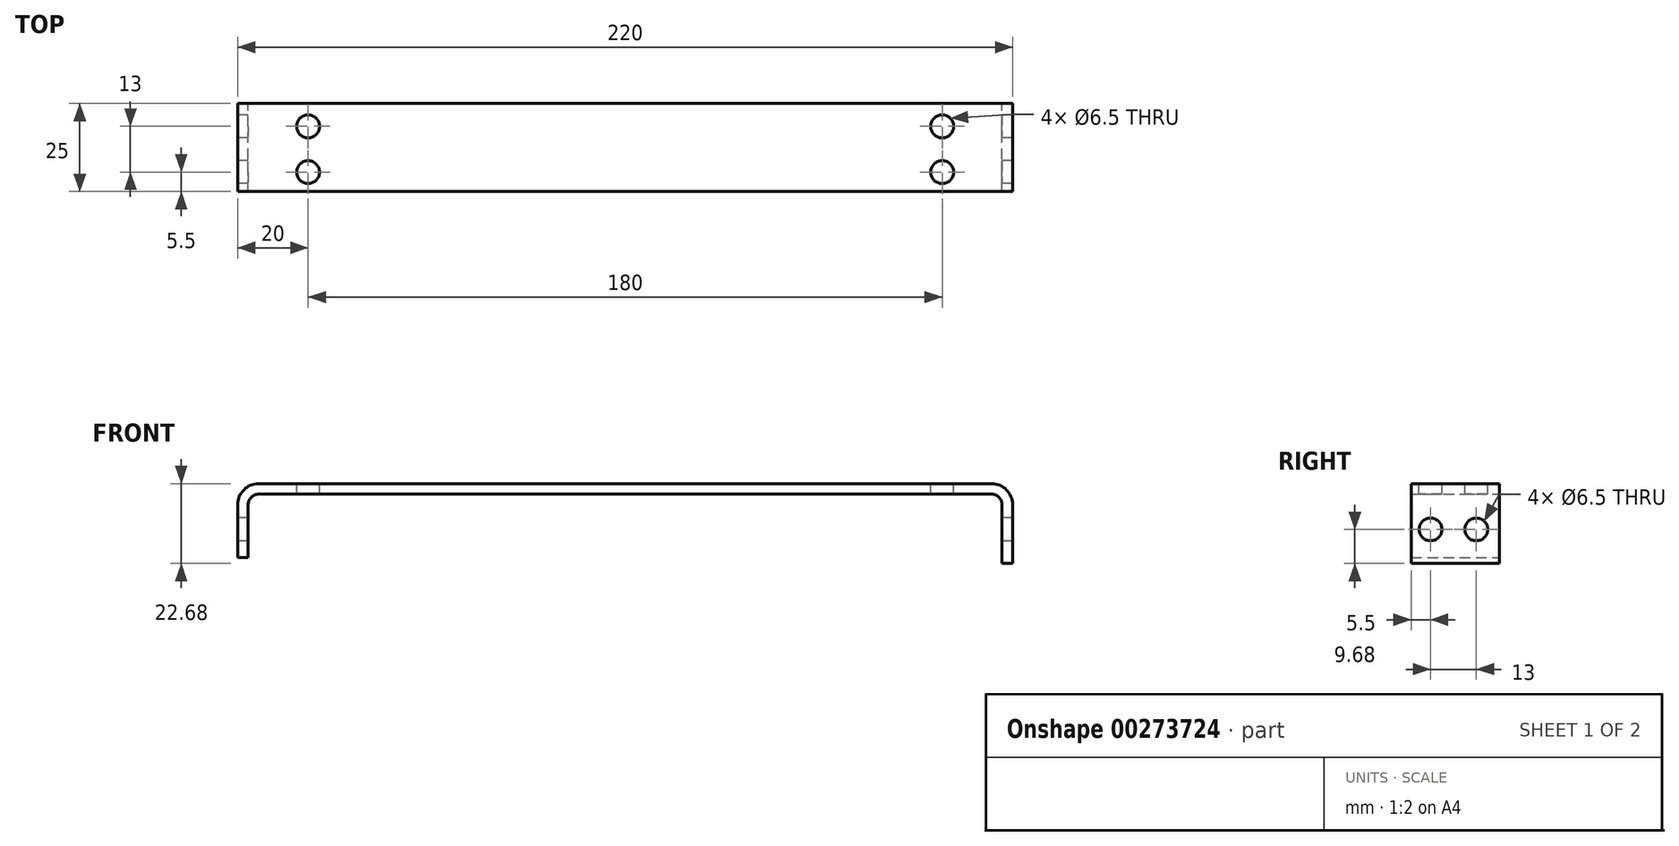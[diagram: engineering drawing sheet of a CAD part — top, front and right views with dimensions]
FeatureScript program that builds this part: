
annotation { "Feature Type Name" : "Feature", "Feature Type Description" : "" }
export const myFeature = defineFeature(function(context is Context, id is Id, definition is map)
    precondition{}
    {
        {
            var Q0;
            Q0=qCreatedBy(makeId("Front.planeOp"),FACE);
            var sketch = newSketch(context, id + "F0", { "sketchPlane" : qUnion([Q0])});
            skLineSegment(sketch, "E0.bottom", {"start": v(-110, 1.5) * mm, "end": v(110, 1.5) * mm});
            skLineSegment(sketch, "E0.top", {"start": v(-110, -1.5) * mm, "end": v(110, -1.5) * mm});
            skLineSegment(sketch, "E0.left", {"start": v(-110, 1.5) * mm, "end": v(-110, -1.5) * mm});
            skLineSegment(sketch, "E0.right", {"start": v(110, 1.5) * mm, "end": v(110, -1.5) * mm});
            skPoint(sketch, "E0.middle", {"position": v(0, 0) * mm});
            skLineSegment(sketch, "E1.bottom", {"start": v(-110, -1.5) * mm, "end": v(-107, -1.5) * mm});
            skLineSegment(sketch, "E1.top", {"start": v(-110, -19.5) * mm, "end": v(-107, -19.5) * mm});
            skLineSegment(sketch, "E1.left", {"start": v(-110, -1.5) * mm, "end": v(-110, -19.5) * mm});
            skLineSegment(sketch, "E1.right", {"start": v(-107, -1.5) * mm, "end": v(-107, -19.5) * mm});
            skLineSegment(sketch, "E2.bottom", {"start": v(110, -1.5) * mm, "end": v(107, -1.5) * mm});
            skLineSegment(sketch, "E2.top", {"start": v(110, -21.18) * mm, "end": v(107, -21.18) * mm});
            skLineSegment(sketch, "E2.left", {"start": v(110, -1.5) * mm, "end": v(110, -21.18) * mm});
            skLineSegment(sketch, "E2.right", {"start": v(107, -1.5) * mm, "end": v(107, -21.18) * mm});
            skSolve(sketch);
        }
        {
            var Q0;
            Q0 = qSketchRegion(id + "F0", true);
            extrude(context, id + "F1", {"entities" : qUnion([Q0]), "depth" : 25 * mm});
        }
        {
            var Q0;
            Q0=makeQuery(id+"F1.opExtrude","SWEPT_FACE",FACE,{"disambiguationData":[OSD([sQuery(id+"F0.wireOp",EDGE,"E0.bottom")])]});
            var sketch = newSketch(context, id + "F2", { "sketchPlane" : qUnion([Q0])});
            skLineSegment(sketch, "E3", {"start": v(-90, 0) * mm, "end": v(-90, -25) * mm, "construction": true});
            skPoint(sketch, "E4", {"position": v(-90, -6.5) * mm});
            skPoint(sketch, "E5", {"position": v(-90, -19.5) * mm});
            skPoint(sketch, "E6.MirrorP", {"position": v(90, -6.5) * mm});
            skPoint(sketch, "E7.MirrorP", {"position": v(90, -19.5) * mm});
            skSolve(sketch);
        }
        {
            var Q0;
            Q0=makeQuery(id+"F1.opExtrude","SWEPT_FACE",FACE,{"disambiguationData":[OSD([sQuery(id+"F0.wireOp",EDGE,"E0.left"),sQuery(id+"F0.wireOp",EDGE,"E1.left")])]});
            var sketch = newSketch(context, id + "F3", { "sketchPlane" : qUnion([Q0])});
            skLineSegment(sketch, "E8", {"start": v(0, -11.5) * mm, "end": v(25, -11.5) * mm, "construction": true});
            skPoint(sketch, "E9", {"position": v(6.5, -11.5) * mm});
            skPoint(sketch, "E10", {"position": v(19.5, -11.5) * mm});
            skSolve(sketch);
        }
        {
            var Q0;
            Q0=sQuery(id+"F2.wireOp",VERTEX,"E5");
            var Q1;
            Q1=sQuery(id+"F2.wireOp",VERTEX,"E4");
            var Q2;
            Q2=sQuery(id+"F2.wireOp",VERTEX,"E6.MirrorP");
            var Q3;
            Q3=sQuery(id+"F2.wireOp",VERTEX,"E7.MirrorP");
            var Q4;
            Q4=makeQuery(id+"F1.opExtrude","SWEPT_BODY",BODY,{"disambiguationData":[OSD([sQuery(id+"F0.wireOp",EDGE,"E0.bottom"),sQuery(id+"F0.wireOp",EDGE,"E0.top"),sQuery(id+"F0.wireOp",EDGE,"E0.left"),sQuery(id+"F0.wireOp",EDGE,"E0.right"),sQuery(id+"F0.wireOp",EDGE,"E1.top"),sQuery(id+"F0.wireOp",EDGE,"E1.left"),sQuery(id+"F0.wireOp",EDGE,"E1.right"),sQuery(id+"F0.wireOp",EDGE,"E2.top"),sQuery(id+"F0.wireOp",EDGE,"E2.left"),sQuery(id+"F0.wireOp",EDGE,"E2.right")])]});
            hole(context, id + "F4", {"style" : HoleStyle.SIMPLE, "endStyle" : HoleEndStyle.THROUGH, "holeDiameter" : 6.5 * mm, "tappedDepth" : 12 * mm, "tapClearance" : 3, "locations" : qUnion([Q0, Q1, Q2, Q3]), "scope" : qUnion([Q4])});
        }
        {
            var Q0;
            Q0=sQuery(id+"F3.wireOp",VERTEX,"E10");
            var Q1;
            Q1=sQuery(id+"F3.wireOp",VERTEX,"E9");
            var Q2;
            Q2=makeQuery(id+"F1.opExtrude","SWEPT_BODY",BODY,{"disambiguationData":[OSD([sQuery(id+"F0.wireOp",EDGE,"E0.bottom"),sQuery(id+"F0.wireOp",EDGE,"E0.top"),sQuery(id+"F0.wireOp",EDGE,"E0.left"),sQuery(id+"F0.wireOp",EDGE,"E0.right"),sQuery(id+"F0.wireOp",EDGE,"E1.top"),sQuery(id+"F0.wireOp",EDGE,"E1.left"),sQuery(id+"F0.wireOp",EDGE,"E1.right"),sQuery(id+"F0.wireOp",EDGE,"E2.top"),sQuery(id+"F0.wireOp",EDGE,"E2.left"),sQuery(id+"F0.wireOp",EDGE,"E2.right")])]});
            hole(context, id + "F5", {"style" : HoleStyle.SIMPLE, "endStyle" : HoleEndStyle.THROUGH, "holeDiameter" : 6.5 * mm, "tappedDepth" : 12 * mm, "tapClearance" : 3, "locations" : qUnion([Q0, Q1]), "scope" : qUnion([Q2])});
        }
        {
            var Q0;
            Q0=makeQuery(id+"F1.opExtrude","SWEPT_EDGE",EDGE,{"disambiguationData":[OSD([sQuery(id+"F0.wireOp",EDGE,"E0.top"),sQuery(id+"F0.wireOp",EDGE,"E1.bottom"),sQuery(id+"F0.wireOp",EDGE,"E1.right")])]});
            var Q1;
            Q1=makeQuery(id+"F1.opExtrude","SWEPT_EDGE",EDGE,{"disambiguationData":[OSD([sQuery(id+"F0.wireOp",EDGE,"E0.top"),sQuery(id+"F0.wireOp",EDGE,"E2.bottom"),sQuery(id+"F0.wireOp",EDGE,"E2.right")])]});
            fillet(context, id + "F6", {"entities" : qUnion([Q0, Q1]), "radius" : 3 * mm, "tangentPropagation" : true, "allowEdgeOverflow" : false});
        }
        {
            var Q0;
            Q0=makeQuery(id+"F1.opExtrude","SWEPT_EDGE",EDGE,{"disambiguationData":[OSD([sQuery(id+"F0.wireOp",EDGE,"E0.bottom"),sQuery(id+"F0.wireOp",EDGE,"E0.left")])]});
            var Q1;
            Q1=makeQuery(id+"F1.opExtrude","SWEPT_EDGE",EDGE,{"disambiguationData":[OSD([sQuery(id+"F0.wireOp",EDGE,"E0.bottom"),sQuery(id+"F0.wireOp",EDGE,"E0.right")])]});
            fillet(context, id + "F7", {"entities" : qUnion([Q0, Q1]), "radius" : 6 * mm, "tangentPropagation" : true, "allowEdgeOverflow" : false});
        }
    });
